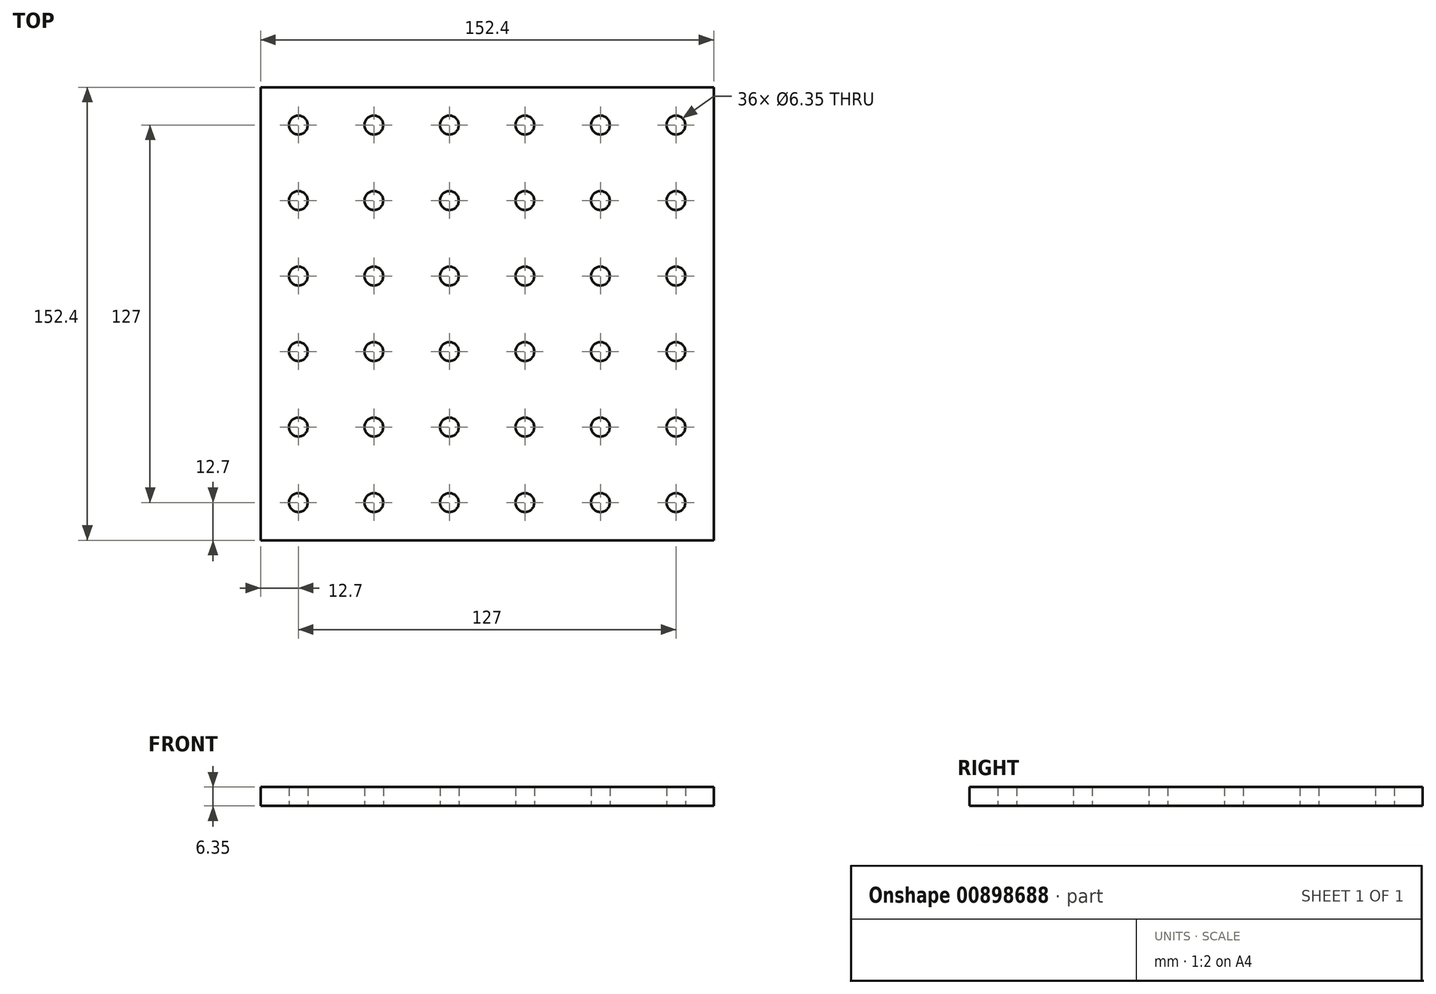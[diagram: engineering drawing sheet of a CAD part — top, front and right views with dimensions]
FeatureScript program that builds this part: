
annotation { "Feature Type Name" : "Feature", "Feature Type Description" : "" }
export const myFeature = defineFeature(function(context is Context, id is Id, definition is map)
    precondition{}
    {
        {
            var Q0;
            Q0=qCreatedBy(makeId("Top.planeOp"),FACE);
            var sketch = newSketch(context, id + "F0", { "sketchPlane" : qUnion([Q0])});
            skLineSegment(sketch, "E0.bottom", {"start": v(-76.2, 76.2) * mm, "end": v(76.2, 76.2) * mm});
            skLineSegment(sketch, "E0.top", {"start": v(-76.2, -76.2) * mm, "end": v(76.2, -76.2) * mm});
            skLineSegment(sketch, "E0.left", {"start": v(-76.2, 76.2) * mm, "end": v(-76.2, -76.2) * mm});
            skLineSegment(sketch, "E0.right", {"start": v(76.2, 76.2) * mm, "end": v(76.2, -76.2) * mm});
            skLineSegment(sketch, "E1", {"start": v(-76.2, 0) * mm, "end": v(76.2, 0) * mm, "construction": true});
            skLineSegment(sketch, "E2", {"start": v(0, 76.2) * mm, "end": v(0, -76.2) * mm, "construction": true});
            skCircle(sketch, "E3", {"center": v(-63.5, -63.5) * mm, "radius": 3.18 * mm});
            skCircle(sketch, "E4.0.1.0", {"center": v(-63.5, -38.1) * mm, "radius": 3.18 * mm});
            skCircle(sketch, "E4.0.2.0", {"center": v(-63.5, -12.7) * mm, "radius": 3.18 * mm});
            skCircle(sketch, "E4.0.3.0", {"center": v(-63.5, 12.7) * mm, "radius": 3.18 * mm});
            skCircle(sketch, "E4.0.4.0", {"center": v(-63.5, 38.1) * mm, "radius": 3.18 * mm});
            skCircle(sketch, "E4.0.5.0", {"center": v(-63.5, 63.5) * mm, "radius": 3.18 * mm});
            skCircle(sketch, "E4.1.0.0", {"center": v(-38.1, -63.5) * mm, "radius": 3.18 * mm});
            skCircle(sketch, "E4.1.1.0", {"center": v(-38.1, -38.1) * mm, "radius": 3.18 * mm});
            skCircle(sketch, "E4.1.2.0", {"center": v(-38.1, -12.7) * mm, "radius": 3.18 * mm});
            skCircle(sketch, "E4.1.3.0", {"center": v(-38.1, 12.7) * mm, "radius": 3.18 * mm});
            skCircle(sketch, "E4.1.4.0", {"center": v(-38.1, 38.1) * mm, "radius": 3.18 * mm});
            skCircle(sketch, "E4.1.5.0", {"center": v(-38.1, 63.5) * mm, "radius": 3.18 * mm});
            skCircle(sketch, "E4.2.0.0", {"center": v(-12.7, -63.5) * mm, "radius": 3.18 * mm});
            skCircle(sketch, "E4.2.1.0", {"center": v(-12.7, -38.1) * mm, "radius": 3.18 * mm});
            skCircle(sketch, "E4.2.2.0", {"center": v(-12.7, -12.7) * mm, "radius": 3.18 * mm});
            skCircle(sketch, "E4.2.3.0", {"center": v(-12.7, 12.7) * mm, "radius": 3.18 * mm});
            skCircle(sketch, "E4.2.4.0", {"center": v(-12.7, 38.1) * mm, "radius": 3.18 * mm});
            skCircle(sketch, "E4.2.5.0", {"center": v(-12.7, 63.5) * mm, "radius": 3.18 * mm});
            skCircle(sketch, "E4.3.0.0", {"center": v(12.7, -63.5) * mm, "radius": 3.18 * mm});
            skCircle(sketch, "E4.3.1.0", {"center": v(12.7, -38.1) * mm, "radius": 3.18 * mm});
            skCircle(sketch, "E4.3.2.0", {"center": v(12.7, -12.7) * mm, "radius": 3.18 * mm});
            skCircle(sketch, "E4.3.3.0", {"center": v(12.7, 12.7) * mm, "radius": 3.18 * mm});
            skCircle(sketch, "E4.3.4.0", {"center": v(12.7, 38.1) * mm, "radius": 3.18 * mm});
            skCircle(sketch, "E4.3.5.0", {"center": v(12.7, 63.5) * mm, "radius": 3.18 * mm});
            skCircle(sketch, "E4.4.0.0", {"center": v(38.1, -63.5) * mm, "radius": 3.18 * mm});
            skCircle(sketch, "E4.4.1.0", {"center": v(38.1, -38.1) * mm, "radius": 3.18 * mm});
            skCircle(sketch, "E4.4.2.0", {"center": v(38.1, -12.7) * mm, "radius": 3.18 * mm});
            skCircle(sketch, "E4.4.3.0", {"center": v(38.1, 12.7) * mm, "radius": 3.18 * mm});
            skCircle(sketch, "E4.4.4.0", {"center": v(38.1, 38.1) * mm, "radius": 3.18 * mm});
            skCircle(sketch, "E4.4.5.0", {"center": v(38.1, 63.5) * mm, "radius": 3.18 * mm});
            skCircle(sketch, "E4.5.0.0", {"center": v(63.5, -63.5) * mm, "radius": 3.18 * mm});
            skCircle(sketch, "E4.5.1.0", {"center": v(63.5, -38.1) * mm, "radius": 3.18 * mm});
            skCircle(sketch, "E4.5.2.0", {"center": v(63.5, -12.7) * mm, "radius": 3.18 * mm});
            skCircle(sketch, "E4.5.3.0", {"center": v(63.5, 12.7) * mm, "radius": 3.18 * mm});
            skCircle(sketch, "E4.5.4.0", {"center": v(63.5, 38.1) * mm, "radius": 3.18 * mm});
            skCircle(sketch, "E4.5.5.0", {"center": v(63.5, 63.5) * mm, "radius": 3.18 * mm});
            skLineSegment(sketch, "E4.direction1", {"start": v(-63.5, -63.5) * mm, "end": v(-38.1, -63.5) * mm, "construction": true});
            skLineSegment(sketch, "E4.direction2", {"start": v(-63.5, -63.5) * mm, "end": v(-63.5, -38.1) * mm, "construction": true});
            skSolve(sketch);
        }
        {
            var Q0;
            Q0=makeQuery(id+"F0.imprint","IMPRINT",FACE,{"disambiguationData":[TD([[makeQuery(id+"F0.imprint","IMPRINT",EDGE,{"derivedFrom":sQuery(id+"F0.wireOp",EDGE,"E0.bottom")}),-1.0]])]});
            extrude(context, id + "F1", {"entities" : qUnion([Q0]), "depth" : 6.35 * mm, "offsetDistance" : 25.4 * mm});
        }
    });
